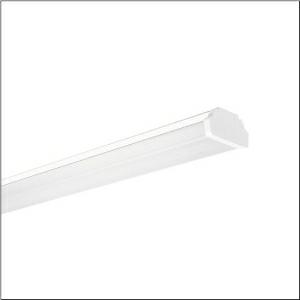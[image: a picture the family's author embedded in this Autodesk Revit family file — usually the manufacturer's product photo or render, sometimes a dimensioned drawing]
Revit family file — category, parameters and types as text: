
# Revit family: dus_r__31_gen_2_53bd812dv4d5d23sl3_1b8c
name_source: partatom
category: Lighting Fixtures
units: mm (PartAtom-declared; Revit-internal decimal feet)

## family parameters
Cut with Voids When Loaded = No
Host = Face
Light Source = No
Part Type = Normal
Room Calculation Point = No
Round Connector Dimension = Use Diameter
Shared = No

## types (1)
- --- (1 x LED, 940 lm, 7.5 W, 4000K)
    Apparent Load = 8 VA
    CIE Flux Codes = 47 80 95 93 100
    Color Rendering = 80
    Color Temperature = 4000K
    Default Elevation = 1800 mm
    Description = DUS® 31 Gen.2, luminaire insert, of sheet steel, coil coated, white, length: 1.535mm, width: 81mm, height: 90mm, 5x system unit, system units: 307mm, LED rated luminous flux: 13.680lm, light colour: 840, control gear: DALI 2, with plug, 6-pole, with phase selection (L1, L2), mains connection: 220..240V, AC, 50/60Hz, rated input power: 79W, for emergency light function, charging phase on L3 (wire number 3), through-wiring accessed according to module size, converter,control gear: single battery element, battery: LiFePO4, 9Ah, primary optical cover: cover, of PMMA, light emission: direct distribution, primary light characteristic: symmetric, protection rating (complete): IP20, protection rating (LED compartment): IP50, insulation class (complete): insulation class I (protective earthing), certification: CE, UKCA, impact resistance: IK03, permissible ambient temperature for indoor applications: +5..+35°C, standard: EN 60598-2-22, corresponds to IFS (International Featured Standards) requirements for safety and quality in the food industry, reducing of maximum allowable ambient temperature of 5°C with ceiling mounting, packaging unit: 1 piece
    Height = 95 mm
    Lamp = 1 x LED
    Lamp Light Flux = 940 lm
    Lamp Power = 7.5 W
    Lamp count = 1
    Length = 1535 mm
    Luminous efficacy = 125 lm/W
    Manufacturer = Siteco
    ModVariant = No
    Model = 53BD812DV4D5D23SL3
    Mounting Place = Ceiling
    Mounting Type = Pendant
    Number of Poles = 1
    OnlyDefault = Yes
    Power Factor = 1
    Product Name = DUS® 31 Gen.2
    Product group = luminaire insert | ceiling pendant
    ProductGroupID = 902
    Protection Class = Protection class I
    Protection Degree = IP 20
    RLX_Detail_Level = 1
    RLX_Emergency_Light_Flux = 0 lm
    RLX_Emergency_Type = 0
    RLX_Emergency_Type_DB = No
    RlxData = <blob elided: 32525 chars, md5=c9f07866>
    Socket = socket
    Standby Power = 0 W
    System Light Flux = 940 lm
    System Power = 8 W
    Type Comments = : emergency light operation: 3 h
    Type Image = l_1319596.jpg
    URL = http://relux.com
    VarID = @adj_042189
    Voltage = 0 V
    Weight = 0.00 kg
    Width = 81 mm

## geometry (parser evidence)
native form markers: Blend x4, Sweep x12
no freeform markers — native parametric forms only
